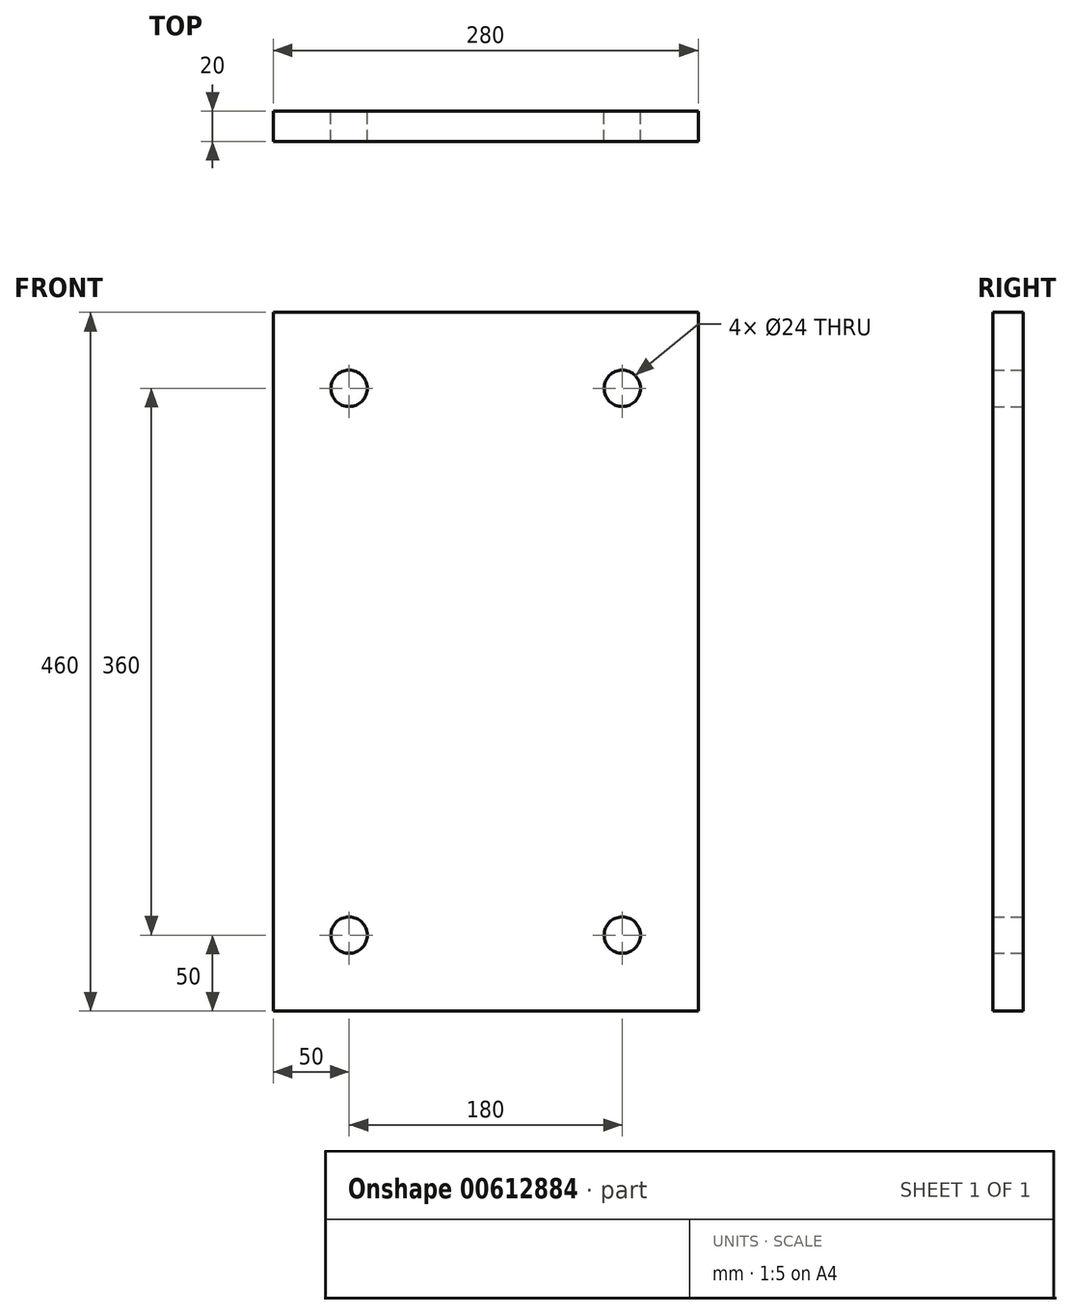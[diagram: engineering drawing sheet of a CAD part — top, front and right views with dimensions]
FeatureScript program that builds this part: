
annotation { "Feature Type Name" : "Feature", "Feature Type Description" : "" }
export const myFeature = defineFeature(function(context is Context, id is Id, definition is map)
    precondition{}
    {
        {
            var Q0;
            Q0=qCreatedBy(makeId("Front.planeOp"),FACE);
            var sketch = newSketch(context, id + "F0", { "sketchPlane" : qUnion([Q0])});
            skLineSegment(sketch, "E0.bottom", {"start": v(140, 230) * mm, "end": v(-140, 230) * mm});
            skLineSegment(sketch, "E0.top", {"start": v(140, -230) * mm, "end": v(-140, -230) * mm});
            skLineSegment(sketch, "E0.left", {"start": v(140, 230) * mm, "end": v(140, -230) * mm});
            skLineSegment(sketch, "E0.right", {"start": v(-140, 230) * mm, "end": v(-140, -230) * mm});
            skPoint(sketch, "E0.middle", {"position": v(0, 0) * mm});
            skCircle(sketch, "E1", {"center": v(-90, 180) * mm, "radius": 12 * mm});
            skCircle(sketch, "E2", {"center": v(90, 180) * mm, "radius": 12 * mm});
            skCircle(sketch, "E3", {"center": v(-90, -180) * mm, "radius": 12 * mm});
            skCircle(sketch, "E4", {"center": v(90, -180) * mm, "radius": 12 * mm});
            skSolve(sketch);
        }
        {
            var Q0;
            Q0=makeQuery(id+"F0.imprint","IMPRINT",FACE,{"disambiguationData":[TD([[makeQuery(id+"F0.imprint","IMPRINT",EDGE,{"derivedFrom":sQuery(id+"F0.wireOp",EDGE,"E0.bottom")}),1.0]])]});
            extrude(context, id + "F1", {"entities" : qUnion([Q0]), "endBound" : BoundingType.SYMMETRIC, "depth" : 20 * mm, "offsetDistance" : 25 * mm});
        }
    });
